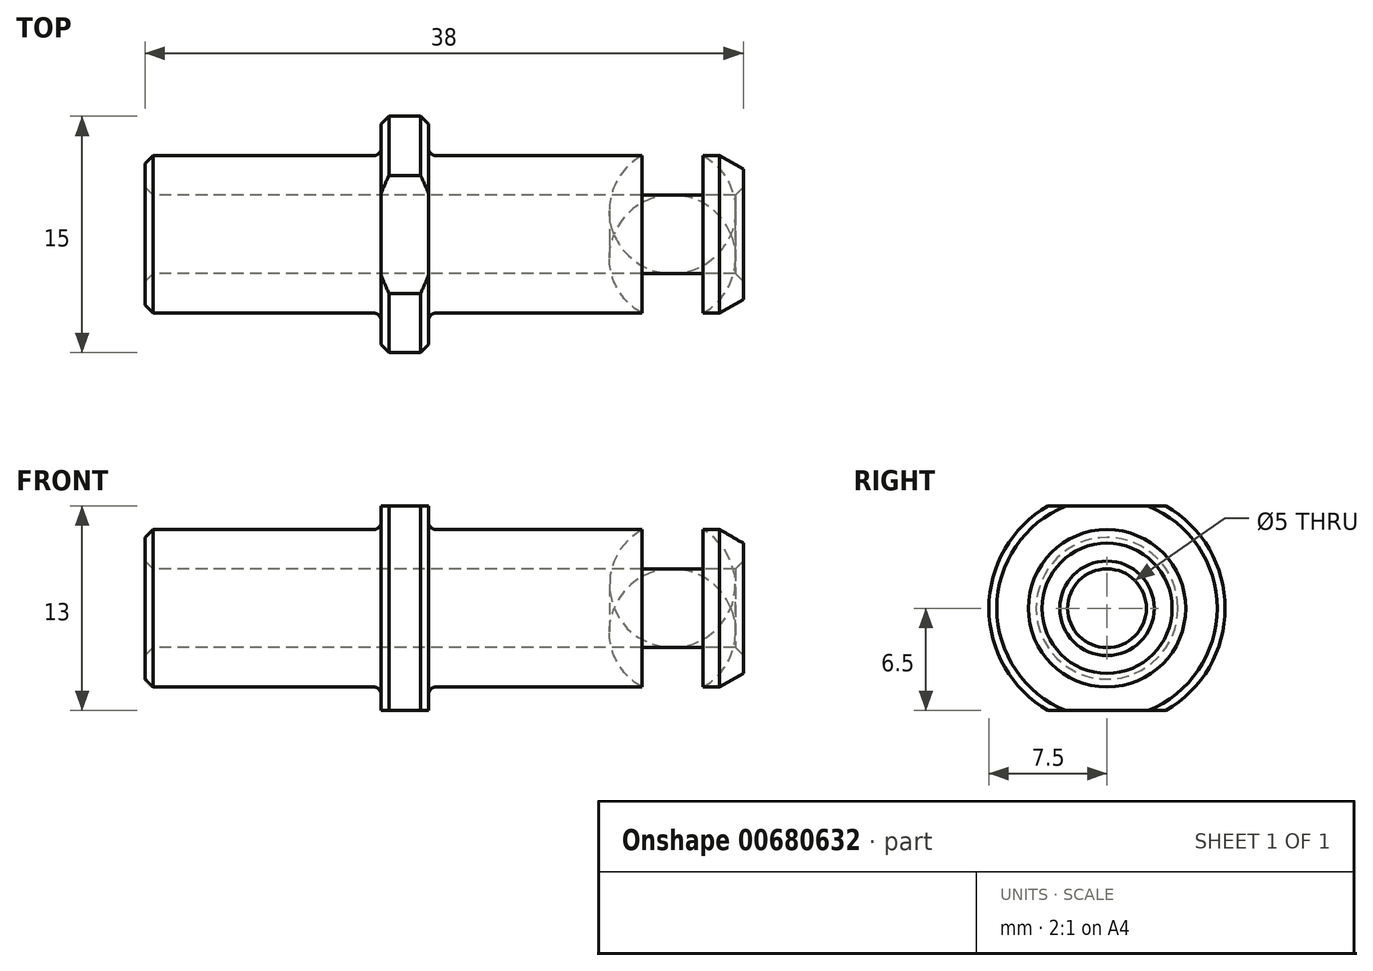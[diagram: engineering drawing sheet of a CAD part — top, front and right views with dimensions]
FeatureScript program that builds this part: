
annotation { "Feature Type Name" : "Feature", "Feature Type Description" : "" }
export const myFeature = defineFeature(function(context is Context, id is Id, definition is map)
    precondition{}
    {
        {
            var Q0;
            Q0=qCreatedBy(makeId("Front.planeOp"),FACE);
            var sketch = newSketch(context, id + "F0", { "sketchPlane" : qUnion([Q0])});
            skLineSegment(sketch, "E0", {"start": v(0, 2.5) * mm, "end": v(38, 2.5) * mm});
            skLineSegment(sketch, "E1", {"start": v(38, 2.5) * mm, "end": v(38, 5) * mm});
            skLineSegment(sketch, "E2", {"start": v(38, 5) * mm, "end": v(35.44, 5) * mm});
            skLineSegment(sketch, "E3", {"start": v(18, 5) * mm, "end": v(18, 7.5) * mm});
            skLineSegment(sketch, "E4", {"start": v(18, 7.5) * mm, "end": v(15, 7.5) * mm});
            skLineSegment(sketch, "E5", {"start": v(15, 7.5) * mm, "end": v(15, 5) * mm});
            skLineSegment(sketch, "E6", {"start": v(15, 5) * mm, "end": v(0, 5) * mm});
            skLineSegment(sketch, "E7", {"start": v(0, 5) * mm, "end": v(0, 2.5) * mm});
            skLineSegment(sketch, "E8.trimOffspring", {"start": v(31.56, 5) * mm, "end": v(18, 5) * mm});
            skArc(sketch, "E9.trimOffspring", {"start": v(35.44, 5) * mm, "mid": v(33.5, 5.5) * mm, "end": v(31.56, 5) * mm});
            skLineSegment(sketch, "E10", {"start": v(0, 0) * mm, "end": v(43.64, 0) * mm, "construction": true});
            skSolve(sketch);
        }
        {
            var Q0;
            Q0=makeQuery(id+"F0.imprint","IMPRINT",FACE,{"disambiguationData":[TD([[makeQuery(id+"F0.imprint","IMPRINT",EDGE,{"derivedFrom":sQuery(id+"F0.wireOp",EDGE,"E0")}),1.0]])]});
            var Q1;
            Q1=sQuery(id+"F0.wireOp",EDGE,"E10");
            revolve(context, id + "F1", {"entities" : qUnion([Q0]), "axis" : qUnion([Q1]), "revolveType" : RevolveType.FULL});
        }
        {
            var Q0;
            Q0=makeQuery(id+"F1.opRevolve","SWEPT_EDGE",EDGE,{"disambiguationData":[OSD([sQuery(id+"F0.wireOp",EDGE,"E6"),sQuery(id+"F0.wireOp",EDGE,"E7")])]});
            var Q1;
            Q1=makeQuery(id+"F1.opRevolve","SWEPT_EDGE",EDGE,{"disambiguationData":[OSD([sQuery(id+"F0.wireOp",EDGE,"E3"),sQuery(id+"F0.wireOp",EDGE,"E4")])]});
            var Q2;
            Q2=makeQuery(id+"F1.opRevolve","SWEPT_EDGE",EDGE,{"disambiguationData":[OSD([sQuery(id+"F0.wireOp",EDGE,"E4"),sQuery(id+"F0.wireOp",EDGE,"E5")])]});
            var Q3;
            Q3=makeQuery(id+"F1.opRevolve","SWEPT_EDGE",EDGE,{"disambiguationData":[OSD([sQuery(id+"F0.wireOp",EDGE,"E0"),sQuery(id+"F0.wireOp",EDGE,"E7")])]});
            var Q4;
            Q4=makeQuery(id+"F1.opRevolve","SWEPT_EDGE",EDGE,{"disambiguationData":[OSD([sQuery(id+"F0.wireOp",EDGE,"E0"),sQuery(id+"F0.wireOp",EDGE,"E1")])]});
            chamfer(context, id + "F2", {"entities" : qUnion([Q0, Q1, Q2, Q3, Q4]), "width" : 0.5 * mm, "tangentPropagation" : true});
        }
        {
            var Q0;
            Q0=makeQuery(id+"F1.opRevolve","SWEPT_EDGE",EDGE,{"disambiguationData":[OSD([sQuery(id+"F0.wireOp",EDGE,"E1"),sQuery(id+"F0.wireOp",EDGE,"E2")])]});
            chamfer(context, id + "F3", {"entities" : qUnion([Q0]), "chamferType" : ChamferType.OFFSET_ANGLE, "width" : 1.5 * mm, "oppositeDirection" : false, "angle" : 30 * degree, "tangentPropagation" : true});
        }
        {
            var Q0;
            Q0=makeQuery(id+"F1.opRevolve","SWEPT_EDGE",EDGE,{"disambiguationData":[OSD([sQuery(id+"F0.wireOp",EDGE,"E3"),sQuery(id+"F0.wireOp",EDGE,"E8.trimOffspring")])]});
            var Q1;
            Q1=makeQuery(id+"F1.opRevolve","SWEPT_EDGE",EDGE,{"disambiguationData":[OSD([sQuery(id+"F0.wireOp",EDGE,"E5"),sQuery(id+"F0.wireOp",EDGE,"E6")])]});
            fillet(context, id + "F4", {"entities" : qUnion([Q0, Q1]), "radius" : 0.5 * mm, "tangentPropagation" : true, "allowEdgeOverflow" : false});
        }
        {
            var Q0;
            Q0=qCreatedBy(makeId("Front.planeOp"),FACE);
            var sketch = newSketch(context, id + "F5", { "sketchPlane" : qUnion([Q0])});
            skLineSegment(sketch, "E11.bottom", {"start": v(14.14, 9.29) * mm, "end": v(19.14, 9.29) * mm});
            skLineSegment(sketch, "E11.top", {"start": v(14.14, 6.5) * mm, "end": v(19.14, 6.5) * mm});
            skLineSegment(sketch, "E11.left", {"start": v(14.14, 9.29) * mm, "end": v(14.14, 6.5) * mm});
            skLineSegment(sketch, "E11.right", {"start": v(19.14, 9.29) * mm, "end": v(19.14, 6.5) * mm});
            skLineSegment(sketch, "E12.bottom", {"start": v(14.14, -10.61) * mm, "end": v(19.14, -10.61) * mm});
            skLineSegment(sketch, "E12.top", {"start": v(14.14, -6.5) * mm, "end": v(19.14, -6.5) * mm});
            skLineSegment(sketch, "E12.left", {"start": v(14.14, -10.61) * mm, "end": v(14.14, -6.5) * mm});
            skLineSegment(sketch, "E12.right", {"start": v(19.14, -10.61) * mm, "end": v(19.14, -6.5) * mm});
            skSolve(sketch);
        }
        {
            var Q0;
            Q0=makeQuery(id+"F5.imprint","IMPRINT",FACE,{"disambiguationData":[TD([[makeQuery(id+"F5.imprint","IMPRINT",EDGE,{"derivedFrom":sQuery(id+"F5.wireOp",EDGE,"E11.bottom")}),-1.0]])]});
            var Q1;
            Q1=makeQuery(id+"F5.imprint","IMPRINT",FACE,{"disambiguationData":[TD([[makeQuery(id+"F5.imprint","IMPRINT",EDGE,{"derivedFrom":sQuery(id+"F5.wireOp",EDGE,"E12.bottom")}),1.0]])]});
            extrude(context, id + "F6", {"entities" : qUnion([Q0, Q1]), "operationType" : NewBodyOperationType.REMOVE, "endBound" : BoundingType.SYMMETRIC, "oppositeDirection" : true, "depth" : 25 * mm, "offsetDistance" : 25 * mm});
        }
    });
